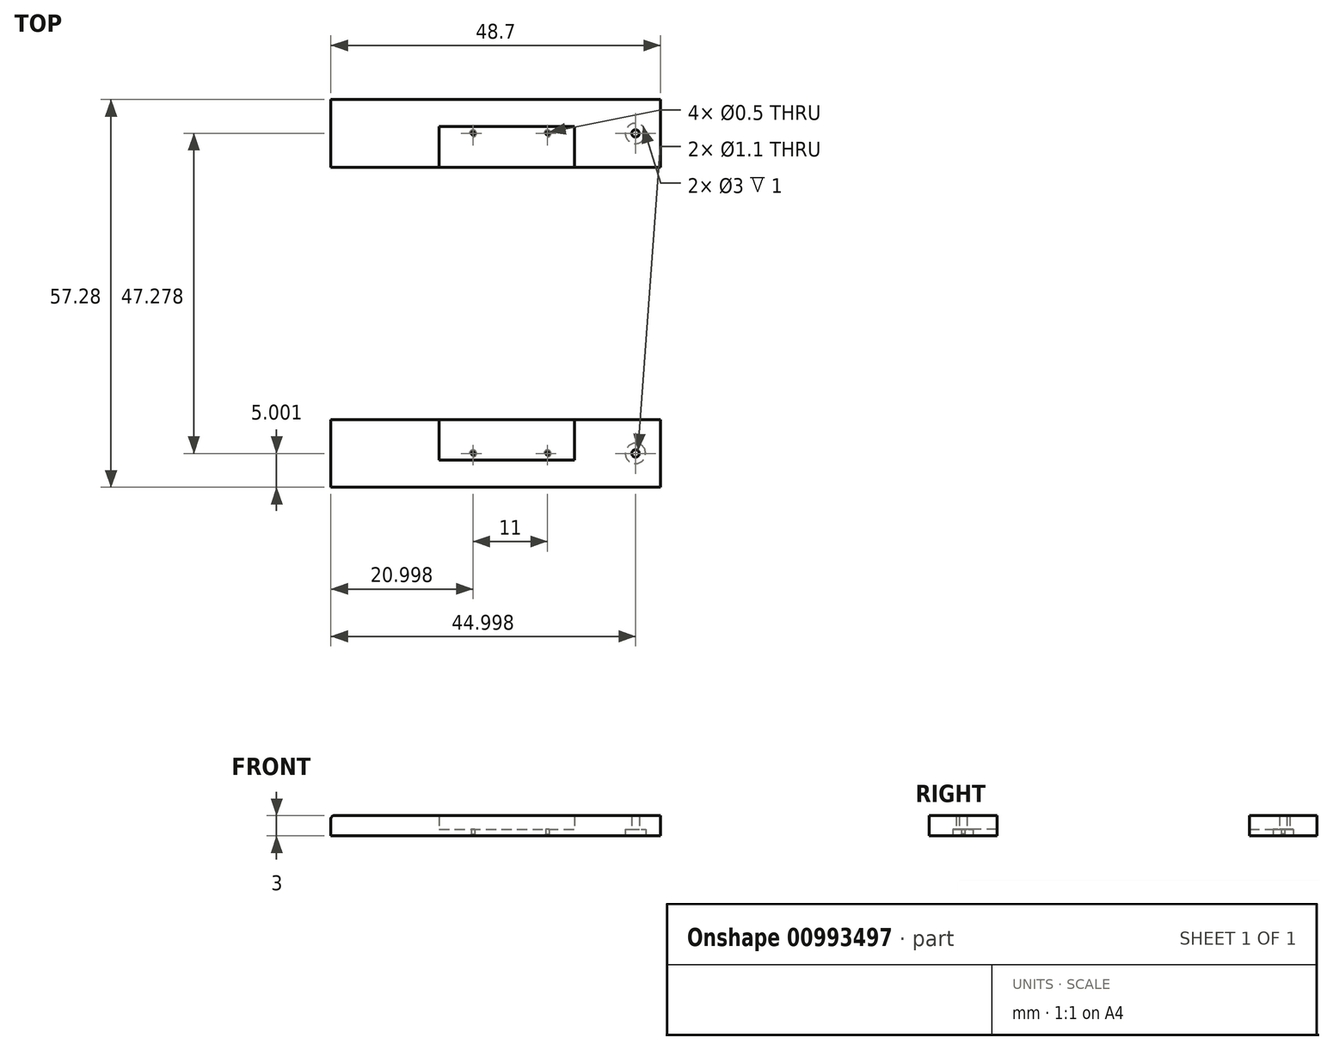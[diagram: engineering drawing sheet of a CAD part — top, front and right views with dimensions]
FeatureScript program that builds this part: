
annotation { "Feature Type Name" : "Feature", "Feature Type Description" : "" }
export const myFeature = defineFeature(function(context is Context, id is Id, definition is map)
    precondition{}
    {
        {
            var Q0;
            Q0=qCreatedBy(makeId("Top.planeOp"),FACE);
            var sketch = newSketch(context, id + "F0", { "sketchPlane" : qUnion([Q0])});
            skLineSegment(sketch, "E0", {"start": v(-44.36, 18.64) * mm, "end": v(-44.36, 28.64) * mm});
            skLineSegment(sketch, "E1", {"start": v(-44.36, 28.64) * mm, "end": v(4.34, 28.64) * mm});
            skLineSegment(sketch, "E2", {"start": v(4.34, 28.64) * mm, "end": v(4.34, 18.64) * mm});
            skLineSegment(sketch, "E3", {"start": v(4.34, 18.64) * mm, "end": v(-44.36, 18.64) * mm});
            skLineSegment(sketch, "E4", {"start": v(-44.36, 18.64) * mm, "end": v(-28.36, 18.64) * mm});
            skLineSegment(sketch, "E5", {"start": v(-28.36, 18.64) * mm, "end": v(-28.36, 24.64) * mm});
            skLineSegment(sketch, "E6", {"start": v(-28.36, 24.64) * mm, "end": v(-8.36, 24.64) * mm});
            skLineSegment(sketch, "E7", {"start": v(-8.36, 24.64) * mm, "end": v(-8.36, 18.64) * mm});
            skLineSegment(sketch, "E8", {"start": v(-8.36, 18.64) * mm, "end": v(-28.36, 18.64) * mm});
            skPoint(sketch, "E9", {"position": v(-23.36, 23.64) * mm});
            skPoint(sketch, "E10", {"position": v(-12.36, 23.64) * mm});
            skPoint(sketch, "E11", {"position": v(0.64, 23.64) * mm});
            skSolve(sketch);
        }
        {
            var Q0;
            Q0=makeQuery(id+"F0.imprint","IMPRINT",FACE,{"disambiguationData":[TD([[makeQuery(id+"F0.imprint","IMPRINT",EDGE,{"derivedFrom":sQuery(id+"F0.wireOp",EDGE,"E0")}),-1.0]])]});
            extrude(context, id + "F1", {"entities" : qUnion([Q0]), "depth" : 3 * mm, "offsetDistance" : 25 * mm});
        }
        {
            var Q0;
            Q0=makeQuery(id+"F0.imprint","IMPRINT",FACE,{"disambiguationData":[TD([[makeQuery(id+"F0.imprint","IMPRINT",EDGE,{"derivedFrom":sQuery(id+"F0.wireOp",EDGE,"E5")}),-1.0]])]});
            extrude(context, id + "F2", {"entities" : qUnion([Q0]), "operationType" : NewBodyOperationType.ADD, "depth" : 1 * mm, "offsetDistance" : 25 * mm});
        }
        {
            var Q0;
            Q0=sQuery(id+"F0.wireOp",VERTEX,"E9");
            var Q1;
            Q1=sQuery(id+"F0.wireOp",VERTEX,"E10");
            var Q2;
            Q2=makeQuery(id+"F1.opExtrude","SWEPT_BODY",BODY,{"disambiguationData":[OSD([sQuery(id+"F0.wireOp",EDGE,"E0"),sQuery(id+"F0.wireOp",EDGE,"E1"),sQuery(id+"F0.wireOp",EDGE,"E2"),sQuery(id+"F0.wireOp",EDGE,"E3"),sQuery(id+"F0.wireOp",EDGE,"E4"),sQuery(id+"F0.wireOp",EDGE,"E5"),sQuery(id+"F0.wireOp",EDGE,"E6"),sQuery(id+"F0.wireOp",EDGE,"E7")])]});
            hole(context, id + "F3", {"style" : HoleStyle.C_SINK, "endStyle" : HoleEndStyle.THROUGH, "oppositeDirection" : true, "holeDiameter" : 0.5 * mm, "cSinkDiameter" : 1 * mm, "cSinkAngle" : 90 * degree, "majorDiameter" : 5 * mm, "isTappedThrough" : true, "tappedDepth" : 12 * mm, "tapClearance" : 3, "locations" : qUnion([Q0, Q1]), "scope" : qUnion([Q2])});
        }
        {
            var Q0;
            Q0=sQuery(id+"F0.wireOp",VERTEX,"E11");
            var Q1;
            Q1=makeQuery(id+"F1.opExtrude","SWEPT_BODY",BODY,{"disambiguationData":[OSD([sQuery(id+"F0.wireOp",EDGE,"E0"),sQuery(id+"F0.wireOp",EDGE,"E1"),sQuery(id+"F0.wireOp",EDGE,"E2"),sQuery(id+"F0.wireOp",EDGE,"E3"),sQuery(id+"F0.wireOp",EDGE,"E4"),sQuery(id+"F0.wireOp",EDGE,"E5"),sQuery(id+"F0.wireOp",EDGE,"E6"),sQuery(id+"F0.wireOp",EDGE,"E7")])]});
            hole(context, id + "F4", {"style" : HoleStyle.C_BORE, "endStyle" : HoleEndStyle.THROUGH, "oppositeDirection" : true, "holeDiameter" : 1.1 * mm, "cBoreDiameter" : 3 * mm, "cBoreDepth" : 1 * mm, "majorDiameter" : 5 * mm, "isTappedThrough" : true, "tappedDepth" : 12 * mm, "tapClearance" : 3, "locations" : qUnion([Q0]), "scope" : qUnion([Q1])});
        }
        {
            var Q0;
            Q0=makeQuery(id+"F1.opExtrude","CAP_EDGE",EDGE,{"disambiguationData":[OSD([sQuery(id+"F0.wireOp",EDGE,"E0")])],"isStart":false});
            fillet(context, id + "F5", {"entities" : qUnion([Q0]), "radius" : 0.5 * mm, "tangentPropagation" : true, "allowEdgeOverflow" : false});
        }
        {
            var Q0;
            Q0=makeQuery(id+"F1.opExtrude","SWEPT_BODY",BODY,{"disambiguationData":[OSD([sQuery(id+"F0.wireOp",EDGE,"E0"),sQuery(id+"F0.wireOp",EDGE,"E1"),sQuery(id+"F0.wireOp",EDGE,"E2"),sQuery(id+"F0.wireOp",EDGE,"E3"),sQuery(id+"F0.wireOp",EDGE,"E4"),sQuery(id+"F0.wireOp",EDGE,"E5"),sQuery(id+"F0.wireOp",EDGE,"E6"),sQuery(id+"F0.wireOp",EDGE,"E7")])]});
            var Q1;
            Q1=qCreatedBy(makeId("Front.planeOp"),FACE);
            mirror(context, id + "F6", {"entities" : qUnion([Q0]), "mirrorPlane" : qUnion([Q1])});
        }
    });
